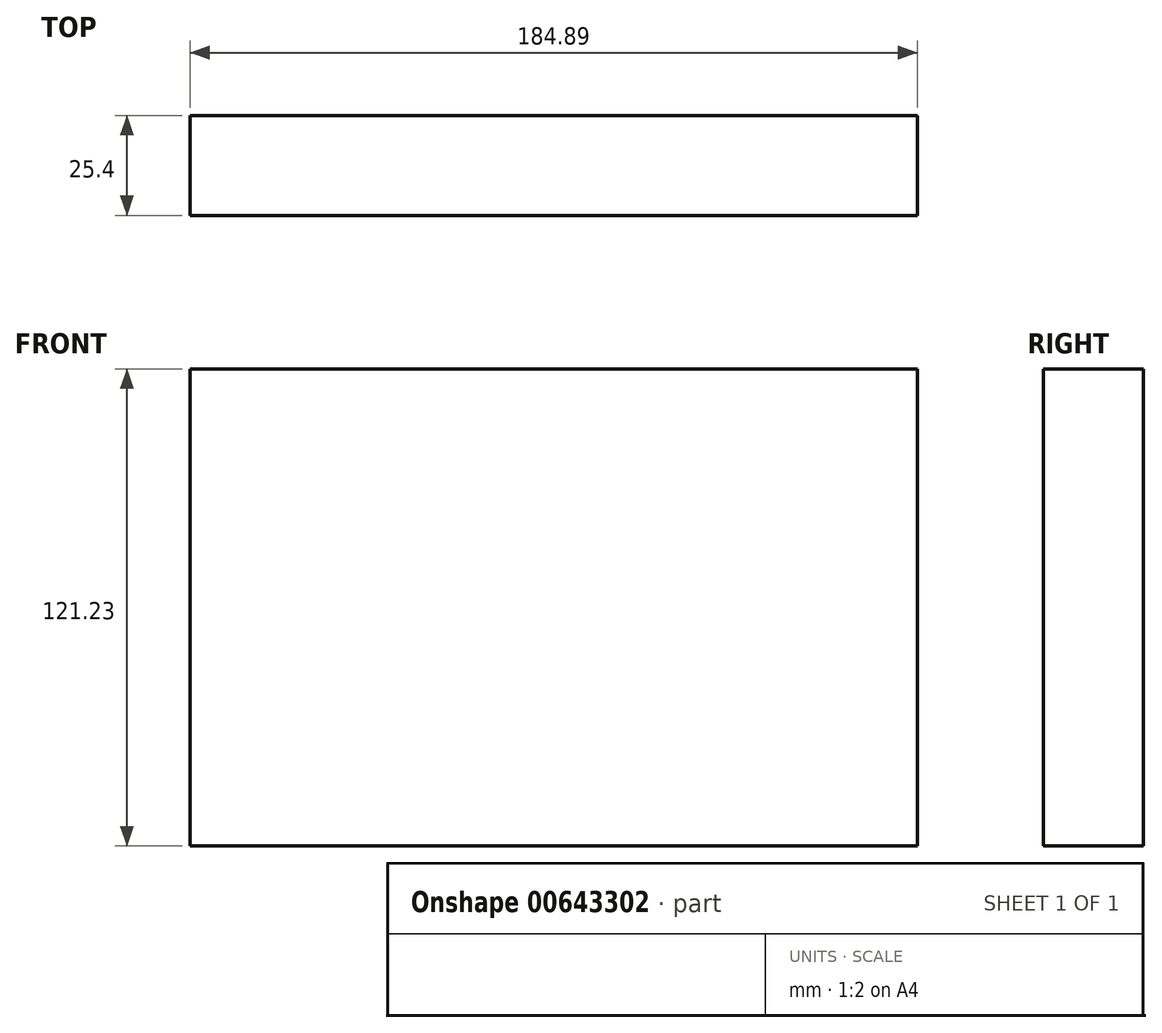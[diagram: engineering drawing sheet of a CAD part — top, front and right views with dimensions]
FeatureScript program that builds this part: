
annotation { "Feature Type Name" : "Feature", "Feature Type Description" : "" }
export const myFeature = defineFeature(function(context is Context, id is Id, definition is map)
    precondition{}
    {
        {
            var Q0;
            Q0=qCreatedBy(makeId("Front.planeOp"),FACE);
            var sketch = newSketch(context, id + "F0", { "sketchPlane" : qUnion([Q0])});
            skLineSegment(sketch, "E0.bottom", {"start": v(-94.63, 65.44) * mm, "end": v(90.26, 65.44) * mm});
            skLineSegment(sketch, "E0.top", {"start": v(-94.63, -55.79) * mm, "end": v(90.26, -55.79) * mm});
            skLineSegment(sketch, "E0.left", {"start": v(-94.63, 65.44) * mm, "end": v(-94.63, -55.79) * mm});
            skLineSegment(sketch, "E0.right", {"start": v(90.26, 65.44) * mm, "end": v(90.26, -55.79) * mm});
            skSolve(sketch);
        }
        {
            var Q0;
            Q0=makeQuery(id+"F0.imprint","IMPRINT",FACE,{"disambiguationData":[TD([[makeQuery(id+"F0.imprint","IMPRINT",EDGE,{"derivedFrom":sQuery(id+"F0.wireOp",EDGE,"E0.bottom")}),-1.0]])]});
            extrude(context, id + "F1", {"entities" : qUnion([Q0]), "depth" : 25.4 * mm, "offsetDistance" : 25.4 * mm});
        }
    });
